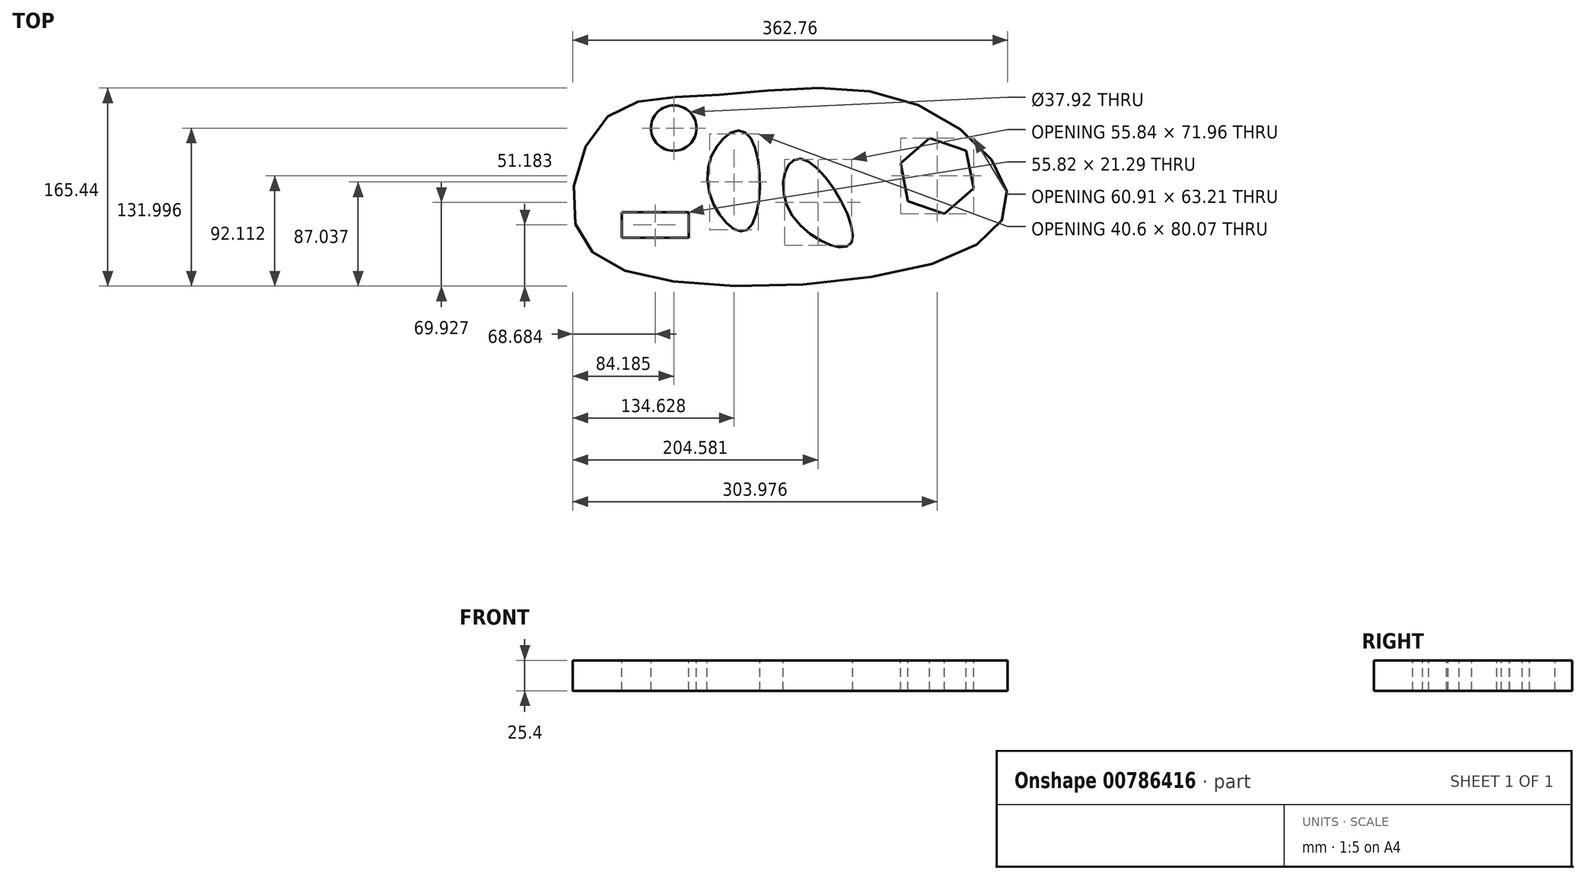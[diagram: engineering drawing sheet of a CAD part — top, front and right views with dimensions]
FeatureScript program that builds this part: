
annotation { "Feature Type Name" : "Feature", "Feature Type Description" : "" }
export const myFeature = defineFeature(function(context is Context, id is Id, definition is map)
    precondition{}
    {
        {
            var Q0;
            Q0=qCreatedBy(makeId("Top.planeOp"),FACE);
            var sketch = newSketch(context, id + "F0", { "sketchPlane" : qUnion([Q0])});
            skFitSpline(sketch, "E0", {"points": [v(-212.88, -23.85) * mm, v(-187.91, 64.42) * mm, v(-101.87, 83.6) * mm, v(58.18, 80.92) * mm, v(146.45, 6.02) * mm, v(112.12, -46.59) * mm, v(-136.64, -71.1) * mm, v(-212.88, -23.85) * mm]});
            skSolve(sketch);
        }
        {
            var Q0;
            Q0=makeQuery(id+"F0.imprint","IMPRINT",FACE,{"disambiguationData":[TD([[makeQuery(id+"F0.imprint","IMPRINT",EDGE,{"derivedFrom":sQuery(id+"F0.wireOp",EDGE,"E0")}),-1.0]])]});
            extrude(context, id + "F1", {"entities" : qUnion([Q0]), "depth" : 25.4 * mm, "offsetDistance" : 25.4 * mm});
        }
        {
            var Q0;
            Q0=makeQuery(id+"F1.opExtrude","CAP_FACE",FACE,{"disambiguationData":[OSD([sQuery(id+"F0.wireOp",EDGE,"E0")])],"isStart":false});
            var sketch = newSketch(context, id + "F2", { "sketchPlane" : qUnion([Q0])});
            skLineSegment(sketch, "E1.bottom", {"start": v(-174.36, -13.95) * mm, "end": v(-118.54, -13.95) * mm});
            skLineSegment(sketch, "E1.top", {"start": v(-174.36, -35.24) * mm, "end": v(-118.54, -35.24) * mm});
            skLineSegment(sketch, "E1.left", {"start": v(-174.36, -13.95) * mm, "end": v(-174.36, -35.24) * mm});
            skLineSegment(sketch, "E1.right", {"start": v(-118.54, -13.95) * mm, "end": v(-118.54, -35.24) * mm});
            skCircle(sketch, "E2.cCircle", {"center": v(88.85, 16.33) * mm, "radius": 27.89 * mm, "construction": true});
            skLineSegment(sketch, "E2.0", {"start": v(58.4, 26.8) * mm, "end": v(82.68, 47.94) * mm});
            skLineSegment(sketch, "E2.1", {"start": v(82.68, 47.94) * mm, "end": v(113.14, 37.47) * mm});
            skLineSegment(sketch, "E2.2", {"start": v(113.14, 37.47) * mm, "end": v(119.3, 5.87) * mm});
            skLineSegment(sketch, "E2.3", {"start": v(119.3, 5.87) * mm, "end": v(95.01, -15.27) * mm});
            skLineSegment(sketch, "E2.4", {"start": v(95.01, -15.27) * mm, "end": v(64.56, -4.8) * mm});
            skLineSegment(sketch, "E2.5", {"start": v(64.56, -4.8) * mm, "end": v(58.4, 26.8) * mm});
            skPoint(sketch, "E2.0.midPoint", {"position": v(70.54, 37.37) * mm});
            skCircle(sketch, "E3", {"center": v(-130.95, 56.22) * mm, "radius": 18.96 * mm});
            skFitSpline(sketch, "E4", {"points": [v(-69.58, -28.78) * mm, v(-103.01, 16.47) * mm, v(-70.52, 52.12) * mm, v(-69.58, -28.78) * mm]});
            skFitSpline(sketch, "E5", {"points": [v(17.37, -39.4) * mm, v(-35.02, -11.54) * mm, v(-24.41, 30.55) * mm, v(17.37, -39.4) * mm]});
            skSolve(sketch);
        }
        {
            var Q0;
            Q0 = qSketchRegion(id + "F2", true);
            extrude(context, id + "F3", {"entities" : qUnion([Q0]), "operationType" : NewBodyOperationType.REMOVE, "oppositeDirection" : true, "depth" : 25.4 * mm, "offsetDistance" : 25.4 * mm});
        }
    });
